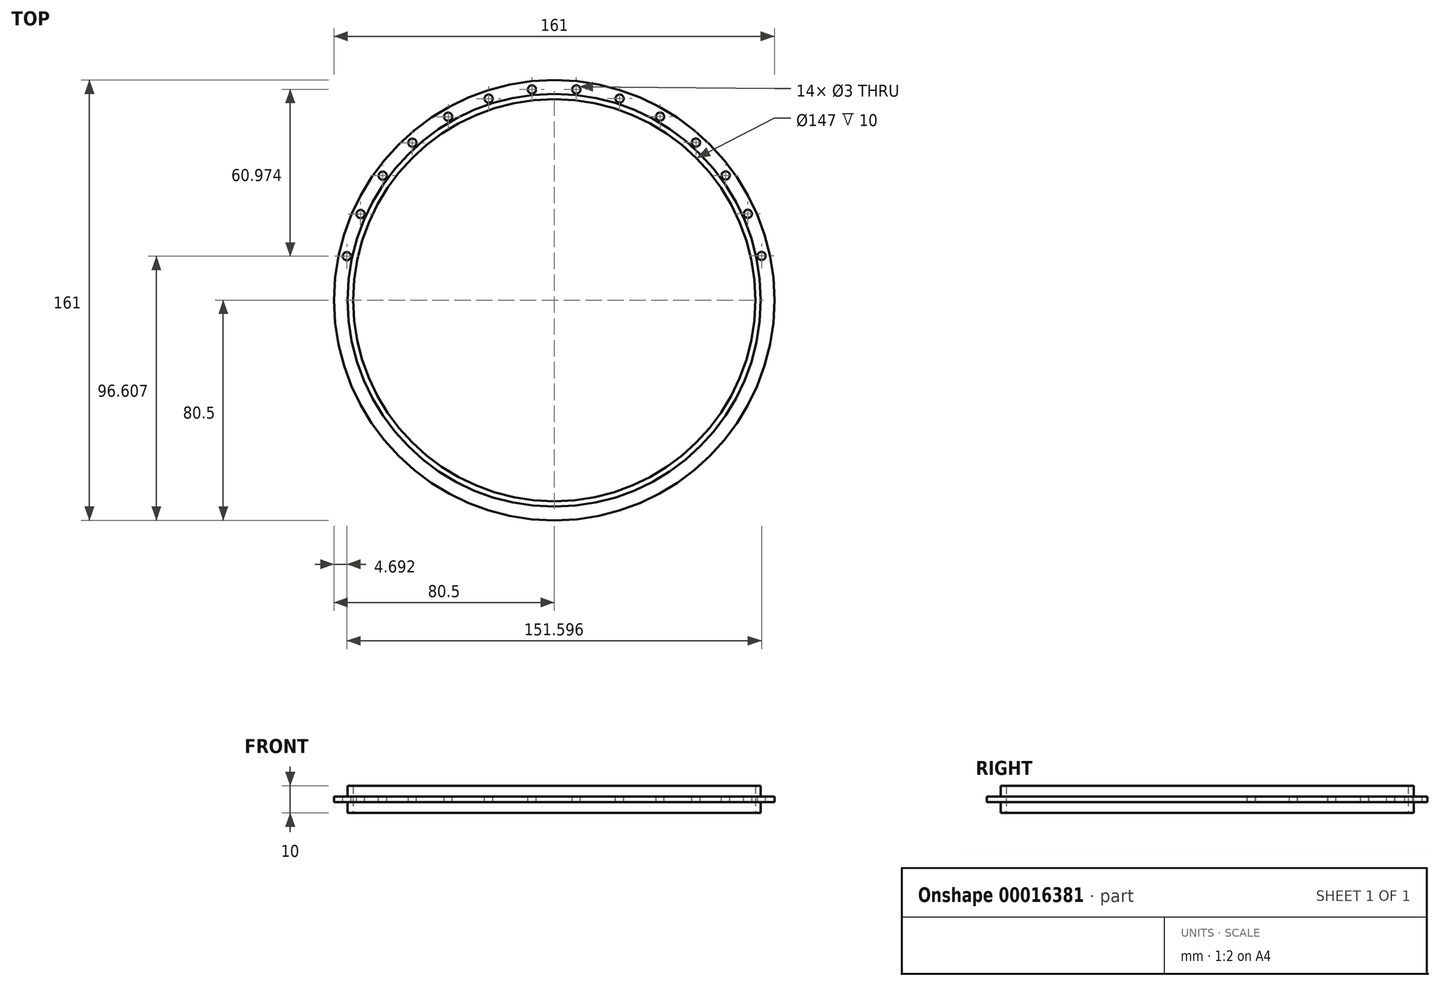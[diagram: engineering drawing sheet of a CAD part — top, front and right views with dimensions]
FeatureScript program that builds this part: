
annotation { "Feature Type Name" : "Feature", "Feature Type Description" : "" }
export const myFeature = defineFeature(function(context is Context, id is Id, definition is map)
    precondition{}
    {
        {
            var Q0;
            Q0=qCreatedBy(makeId("Front.planeOp"),FACE);
            var sketch = newSketch(context, id + "F0", { "sketchPlane" : qUnion([Q0])});
            skLineSegment(sketch, "E0", {"start": v(-75.5, 1) * mm, "end": v(-80.5, 1) * mm});
            skLineSegment(sketch, "E1", {"start": v(-80.5, 1) * mm, "end": v(-80.5, -1) * mm});
            skLineSegment(sketch, "E2", {"start": v(-80.5, -1) * mm, "end": v(-75.5, -1) * mm});
            skLineSegment(sketch, "E3", {"start": v(-75.5, -1) * mm, "end": v(-75.5, -5) * mm});
            skLineSegment(sketch, "E4", {"start": v(-75.5, -5) * mm, "end": v(-73.5, -5) * mm});
            skLineSegment(sketch, "E5", {"start": v(-73.5, -5) * mm, "end": v(-73.5, 5) * mm});
            skLineSegment(sketch, "E6", {"start": v(-73.5, 5) * mm, "end": v(-75.5, 5) * mm});
            skLineSegment(sketch, "E7", {"start": v(-75.5, 5) * mm, "end": v(-75.5, 1) * mm});
            skLineSegment(sketch, "E8", {"start": v(0, -42.11) * mm, "end": v(0, 37.47) * mm, "construction": true});
            skSolve(sketch);
        }
        {
            var Q0;
            Q0 = qSketchRegion(id + "F0", true);
            var Q1;
            Q1=sQuery(id+"F0.wireOp",EDGE,"E8");
            revolve(context, id + "F1", {"entities" : qUnion([Q0]), "axis" : qUnion([Q1]), "revolveType" : RevolveType.FULL});
        }
        {
            var Q0;
            Q0=makeQuery(id+"F1.opRevolve","SWEPT_FACE",FACE,{"disambiguationData":[OSD([sQuery(id+"F0.wireOp",EDGE,"E0")])]});
            var sketch = newSketch(context, id + "F2", { "sketchPlane" : qUnion([Q0])});
            skCircle(sketch, "E9.1.0", {"center": v(-75.8, 16.1) * mm, "radius": 1.5 * mm});
            skCircle(sketch, "E9.2.0", {"center": v(-70.8, 31.51) * mm, "radius": 1.5 * mm});
            skCircle(sketch, "E9.3.0", {"center": v(-62.71, 45.54) * mm, "radius": 1.5 * mm});
            skCircle(sketch, "E9.4.0", {"center": v(-51.88, 57.58) * mm, "radius": 1.5 * mm});
            skCircle(sketch, "E9.5.0", {"center": v(-38.78, 67.1) * mm, "radius": 1.5 * mm});
            skCircle(sketch, "E9.6.0", {"center": v(-23.99, 73.7) * mm, "radius": 1.5 * mm});
            skCircle(sketch, "E9.7.0", {"center": v(-8.15, 77.07) * mm, "radius": 1.5 * mm});
            skCircle(sketch, "E9.8.0", {"center": v(8.05, 77.08) * mm, "radius": 1.5 * mm});
            skCircle(sketch, "E9.9.0", {"center": v(23.9, 73.72) * mm, "radius": 1.5 * mm});
            skCircle(sketch, "E9.10.0", {"center": v(38.7, 67.15) * mm, "radius": 1.5 * mm});
            skCircle(sketch, "E9.11.0", {"center": v(51.8, 57.64) * mm, "radius": 1.5 * mm});
            skCircle(sketch, "E9.12.0", {"center": v(62.65, 45.62) * mm, "radius": 1.5 * mm});
            skCircle(sketch, "E9.13.0", {"center": v(70.77, 31.6) * mm, "radius": 1.5 * mm});
            skCircle(sketch, "E9.14.0", {"center": v(75.79, 16.2) * mm, "radius": 1.5 * mm});
            skPoint(sketch, "E9.center", {"position": v(0, 0) * mm});
            skLineSegment(sketch, "E9.anchor1", {"start": v(0, 0) * mm, "end": v(-77.5, 0) * mm, "construction": true});
            skLineSegment(sketch, "E9.anchor2", {"start": v(0, 0) * mm, "end": v(77.5, 0.1) * mm, "construction": true});
            skSolve(sketch);
        }
        {
            var Q0;
            Q0 = qSketchRegion(id + "F2", true);
            extrude(context, id + "F3", {"entities" : qUnion([Q0]), "operationType" : NewBodyOperationType.REMOVE, "oppositeDirection" : true, "depth" : 25 * mm});
        }
    });
